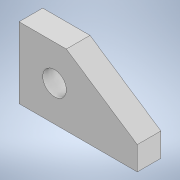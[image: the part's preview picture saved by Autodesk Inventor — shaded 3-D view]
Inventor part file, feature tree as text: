
AUTODESK INVENTOR PART (.ipt)
format: ipt  version: 2021 (Build 250183000, 183)  size: 106,496 bytes
history: native  units: mm
features: sketch x2, other x1, extrude x1, hole x1
ambient origin geometry x8: Origin, YZ Plane, XZ Plane, XY Plane, X Axis, Y Axis, Z Axis, Center Point
bodies: Body1 (feature_tree)
feature tree (5):
  other  "Sólido1"
  extrude  "Extrusão1"  Depth=10.0mm
  hole  "Furo1"  [1 undecoded]
  sketch  "Esboço1"  dims[d0=50.0mm d1=10.0mm]
  sketch  "Esboço2"  dims[d2=30.0mm d3=20.0mm d4=10.0mm d5=0.0mm d6=15.0mm d7=10.0mm d8=6.0mm d9=4.0mm d10=2.0mm d11=90.0deg d12=8.0mm d13=20.594885mm d14=15.0mm]
note: 1 required parameter value undecoded (feature->parameter linkage not recoverable at this tier; creation-order binding heuristic only, values carry confidence <= 0.55)
